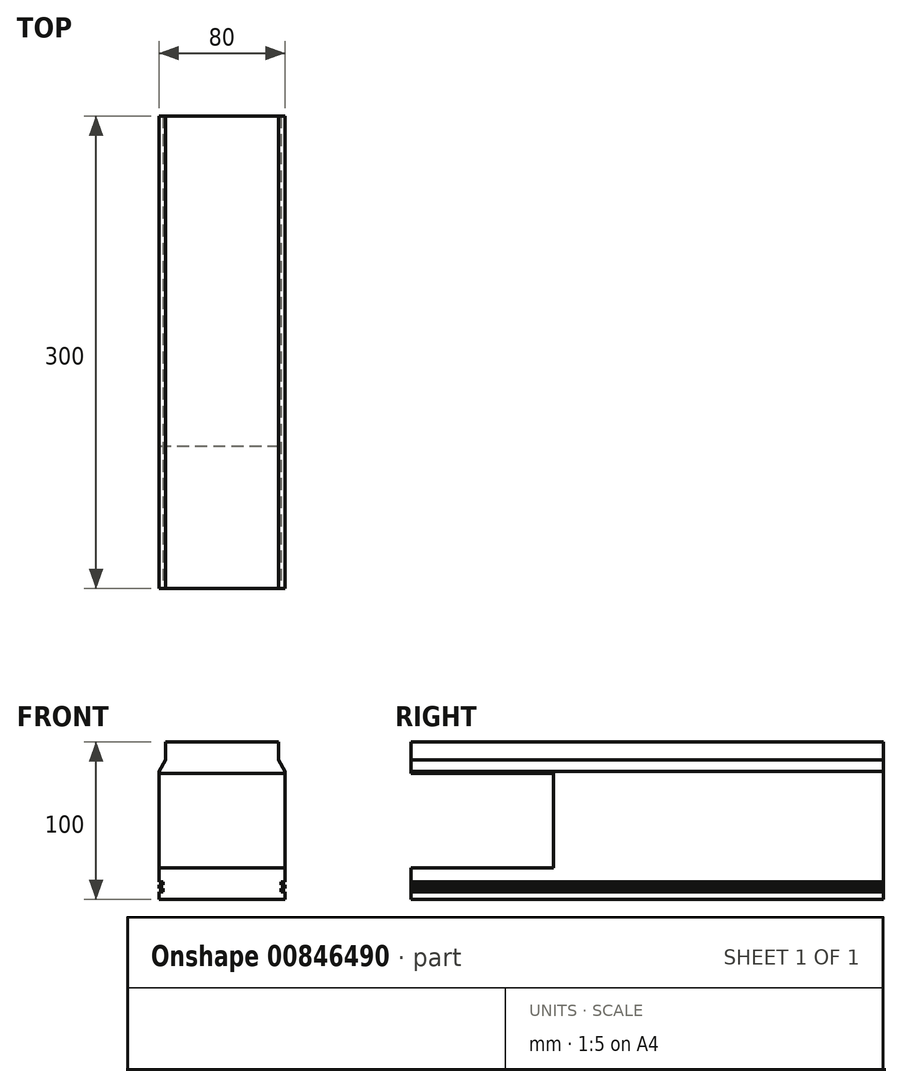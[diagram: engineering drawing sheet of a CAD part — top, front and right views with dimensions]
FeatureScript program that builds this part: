
annotation { "Feature Type Name" : "Feature", "Feature Type Description" : "" }
export const myFeature = defineFeature(function(context is Context, id is Id, definition is map)
    precondition{}
    {
        {
            var Q0;
            Q0=qCreatedBy(makeId("Top.planeOp"),FACE);
            var sketch = newSketch(context, id + "F0", { "sketchPlane" : qUnion([Q0])});
            skLineSegment(sketch, "E0.bottom", {"start": v(40, 150) * mm, "end": v(-40, 150) * mm});
            skLineSegment(sketch, "E0.top", {"start": v(40, -150) * mm, "end": v(-40, -150) * mm});
            skLineSegment(sketch, "E0.left", {"start": v(40, 150) * mm, "end": v(40, -150) * mm});
            skLineSegment(sketch, "E0.right", {"start": v(-40, 150) * mm, "end": v(-40, -150) * mm});
            skPoint(sketch, "E0.middle", {"position": v(0, 0) * mm});
            skSolve(sketch);
        }
        {
            var Q0;
            Q0=makeQuery(id+"F0.imprint","IMPRINT",FACE,{"disambiguationData":[TD([[makeQuery(id+"F0.imprint","IMPRINT",EDGE,{"derivedFrom":sQuery(id+"F0.wireOp",EDGE,"E0.bottom")}),1.0]])]});
            extrude(context, id + "F1", {"entities" : qUnion([Q0]), "depth" : 100 * mm, "offsetDistance" : 25 * mm});
        }
        {
            var Q0;
            Q0=makeQuery(id+"F1.opExtrude","SWEPT_FACE",FACE,{"disambiguationData":[OSD([sQuery(id+"F0.wireOp",EDGE,"E0.top")])]});
            var sketch = newSketch(context, id + "F2", { "sketchPlane" : qUnion([Q0])});
            skLineSegment(sketch, "E1", {"start": v(35.78, 100) * mm, "end": v(35.78, 88.74) * mm});
            skLineSegment(sketch, "E2", {"start": v(35.78, 88.74) * mm, "end": v(40, 81.33) * mm});
            skLineSegment(sketch, "E3", {"start": v(40, 81.33) * mm, "end": v(40, 60.77) * mm});
            skLineSegment(sketch, "E4", {"start": v(40, 60.77) * mm, "end": v(37.4, 60.77) * mm});
            skLineSegment(sketch, "E5", {"start": v(37.4, 60.77) * mm, "end": v(37.4, 31.01) * mm});
            skLineSegment(sketch, "E6", {"start": v(37.4, 31.01) * mm, "end": v(40, 31.01) * mm});
            skLineSegment(sketch, "E7", {"start": v(40, 31.01) * mm, "end": v(40, 0) * mm});
            skLineSegment(sketch, "E8", {"start": v(40, 0) * mm, "end": v(-40, 0) * mm});
            skLineSegment(sketch, "E9.MirrorCS", {"start": v(-35.78, 100) * mm, "end": v(-35.78, 88.74) * mm});
            skLineSegment(sketch, "E10.MirrorCS", {"start": v(-35.78, 88.74) * mm, "end": v(-40, 81.33) * mm});
            skLineSegment(sketch, "E11.MirrorCS", {"start": v(-40, 81.33) * mm, "end": v(-40, 60.77) * mm});
            skLineSegment(sketch, "E12.MirrorCS", {"start": v(-40, 60.77) * mm, "end": v(-37.4, 60.77) * mm});
            skLineSegment(sketch, "E13.MirrorCS", {"start": v(-37.4, 60.77) * mm, "end": v(-37.4, 31.01) * mm});
            skLineSegment(sketch, "E14.MirrorCS", {"start": v(-37.4, 31.01) * mm, "end": v(-40, 31.01) * mm});
            skLineSegment(sketch, "E15.MirrorCS", {"start": v(-40, 31.01) * mm, "end": v(-40, 0) * mm});
            skLineSegment(sketch, "E16.MirrorCS", {"start": v(-40, 0) * mm, "end": v(40, 0) * mm});
            skLineSegment(sketch, "E17", {"start": v(-40, 28.04) * mm, "end": v(-37.4, 28.04) * mm});
            skLineSegment(sketch, "E18", {"start": v(-37.4, 28.04) * mm, "end": v(-37.4, 25.93) * mm});
            skLineSegment(sketch, "E19", {"start": v(-37.4, 25.93) * mm, "end": v(-40, 25.93) * mm});
            skLineSegment(sketch, "E20.MirrorCS", {"start": v(-40, 23.83) * mm, "end": v(-37.4, 23.83) * mm});
            skLineSegment(sketch, "E21.MirrorCS", {"start": v(-37.4, 21.72) * mm, "end": v(-40, 21.72) * mm});
            skLineSegment(sketch, "E22.MirrorCS", {"start": v(-40, 19.62) * mm, "end": v(-37.4, 19.62) * mm});
            skLineSegment(sketch, "E23.MirrorCS", {"start": v(-37.4, 23.83) * mm, "end": v(-37.4, 21.72) * mm});
            skLineSegment(sketch, "E24.MirrorCS", {"start": v(-37.4, 17.51) * mm, "end": v(-40, 17.51) * mm});
            skLineSegment(sketch, "E25.MirrorCS", {"start": v(-40, 15.4) * mm, "end": v(-37.4, 15.4) * mm});
            skLineSegment(sketch, "E26.MirrorCS", {"start": v(-37.4, 13.3) * mm, "end": v(-40, 13.3) * mm});
            skLineSegment(sketch, "E27.MirrorCS", {"start": v(-40, 11.2) * mm, "end": v(-37.4, 11.2) * mm});
            skLineSegment(sketch, "E28.MirrorCS", {"start": v(-37.4, 15.4) * mm, "end": v(-37.4, 13.3) * mm});
            skLineSegment(sketch, "E29.MirrorCS", {"start": v(-37.4, 19.62) * mm, "end": v(-37.4, 17.51) * mm});
            skLineSegment(sketch, "E30.MirrorCS", {"start": v(-37.4, 9.1) * mm, "end": v(-40, 9.1) * mm});
            skLineSegment(sketch, "E31.MirrorCS", {"start": v(-40, 7) * mm, "end": v(-37.4, 7) * mm});
            skLineSegment(sketch, "E32.MirrorCS", {"start": v(-37.4, 4.89) * mm, "end": v(-40, 4.89) * mm});
            skLineSegment(sketch, "E33.MirrorCS", {"start": v(-37.4, 11.2) * mm, "end": v(-37.4, 9.1) * mm});
            skLineSegment(sketch, "E34.MirrorCS", {"start": v(-37.4, 7) * mm, "end": v(-37.4, 4.89) * mm});
            skPoint(sketch, "E35.MirrorCS.end.orphan", {"position": v(-37.4, 25.93) * mm});
            skPoint(sketch, "E35.MirrorCS.start.orphan", {"position": v(-37.4, 23.83) * mm});
            skPoint(sketch, "E36.MirrorCS.end.orphan", {"position": v(-37.4, 21.72) * mm});
            skPoint(sketch, "E36.MirrorCS.start.orphan", {"position": v(-37.4, 19.62) * mm});
            skPoint(sketch, "E37.MirrorCS.end.orphan", {"position": v(-37.4, 17.51) * mm});
            skPoint(sketch, "E37.MirrorCS.start.orphan", {"position": v(-37.4, 15.4) * mm});
            skPoint(sketch, "E38.MirrorCS.end.orphan", {"position": v(-37.4, 13.3) * mm});
            skPoint(sketch, "E38.MirrorCS.start.orphan", {"position": v(-37.4, 11.2) * mm});
            skPoint(sketch, "E39.MirrorCS.end.orphan", {"position": v(-37.4, 9.1) * mm});
            skPoint(sketch, "E39.MirrorCS.start.orphan", {"position": v(-37.4, 7) * mm});
            skLineSegment(sketch, "E40.MirrorCS", {"start": v(37.4, 4.89) * mm, "end": v(40, 4.89) * mm});
            skLineSegment(sketch, "E41.MirrorCS", {"start": v(37.4, 7) * mm, "end": v(37.4, 4.89) * mm});
            skLineSegment(sketch, "E42.MirrorCS", {"start": v(40, 7) * mm, "end": v(37.4, 7) * mm});
            skLineSegment(sketch, "E43.MirrorCS", {"start": v(37.4, 9.1) * mm, "end": v(40, 9.1) * mm});
            skLineSegment(sketch, "E44.MirrorCS", {"start": v(37.4, 11.2) * mm, "end": v(37.4, 9.1) * mm});
            skLineSegment(sketch, "E45.MirrorCS", {"start": v(37.4, 13.3) * mm, "end": v(40, 13.3) * mm});
            skPoint(sketch, "E46.MirrorP", {"position": v(37.4, 13.3) * mm});
            skPoint(sketch, "E47.MirrorP", {"position": v(37.4, 15.4) * mm});
            skLineSegment(sketch, "E48.MirrorCS", {"start": v(37.4, 15.4) * mm, "end": v(37.4, 13.3) * mm});
            skLineSegment(sketch, "E49.MirrorCS", {"start": v(40, 15.4) * mm, "end": v(37.4, 15.4) * mm});
            skLineSegment(sketch, "E50.MirrorCS", {"start": v(37.4, 17.51) * mm, "end": v(40, 17.51) * mm});
            skLineSegment(sketch, "E51.MirrorCS", {"start": v(37.4, 19.62) * mm, "end": v(37.4, 17.51) * mm});
            skLineSegment(sketch, "E52.MirrorCS", {"start": v(40, 19.62) * mm, "end": v(37.4, 19.62) * mm});
            skLineSegment(sketch, "E53.MirrorCS", {"start": v(37.4, 21.72) * mm, "end": v(40, 21.72) * mm});
            skLineSegment(sketch, "E54.MirrorCS", {"start": v(40, 23.83) * mm, "end": v(37.4, 23.83) * mm});
            skLineSegment(sketch, "E55.MirrorCS", {"start": v(37.4, 23.83) * mm, "end": v(37.4, 21.72) * mm});
            skLineSegment(sketch, "E56.MirrorCS", {"start": v(37.4, 25.93) * mm, "end": v(40, 25.93) * mm});
            skLineSegment(sketch, "E57.MirrorCS", {"start": v(37.4, 28.04) * mm, "end": v(37.4, 25.93) * mm});
            skLineSegment(sketch, "E58.MirrorCS", {"start": v(40, 28.04) * mm, "end": v(37.4, 28.04) * mm});
            skLineSegment(sketch, "E59.MirrorCS", {"start": v(40, 11.2) * mm, "end": v(37.4, 11.2) * mm});
            skSolve(sketch);
        }
        {
            var Q0;
            Q0=makeQuery(id+"F1.opExtrude","SWEPT_FACE",FACE,{"disambiguationData":[OSD([sQuery(id+"F0.wireOp",EDGE,"E0.left")])]});
            var sketch = newSketch(context, id + "F3", { "sketchPlane" : qUnion([Q0])});
            skLineSegment(sketch, "E60.bottom", {"start": v(-59.49, 80.07) * mm, "end": v(-240.51, 80.07) * mm});
            skLineSegment(sketch, "E60.top", {"start": v(-59.49, 19.93) * mm, "end": v(-240.51, 19.93) * mm});
            skLineSegment(sketch, "E60.left", {"start": v(-59.49, 80.07) * mm, "end": v(-59.49, 19.93) * mm});
            skLineSegment(sketch, "E60.right", {"start": v(-240.51, 80.07) * mm, "end": v(-240.51, 19.93) * mm});
            skPoint(sketch, "E60.middle", {"position": v(-150, 50) * mm});
            skSolve(sketch);
        }
        {
            var Q0;
            {var subQ0=sQuery(id+"F3.wireOp",EDGE,"E60.left");Q0=makeQuery(id+"F3.imprint","IMPRINT",FACE,{"disambiguationData":[TD([[makeQuery(id+"F3.imprint","IMPRINT",EDGE,{"derivedFrom":subQ0}),-1.0]])]});}
            extrude(context, id + "F4", {"entities" : qUnion([Q0]), "operationType" : NewBodyOperationType.REMOVE, "oppositeDirection" : true, "depth" : 128 * mm, "offsetDistance" : 25 * mm});
        }
        {
            var Q0;
            {var subQ0=sQuery(id+"F2.wireOp",EDGE,"E1");Q0=makeQuery(id+"F2.imprint","IMPRINT",FACE,{"disambiguationData":[TD([[makeQuery(id+"F2.imprint","IMPRINT",EDGE,{"derivedFrom":subQ0}),1.0]])]});}
            var Q1;
            {var subQ0=sQuery(id+"F2.wireOp",EDGE,"E9.MirrorCS");Q1=makeQuery(id+"F2.imprint","IMPRINT",FACE,{"disambiguationData":[TD([[makeQuery(id+"F2.imprint","IMPRINT",EDGE,{"derivedFrom":subQ0}),-1.0]])]});}
            var Q2;
            {var subQ0=sQuery(id+"F2.wireOp",EDGE,"E43.MirrorCS");Q2=makeQuery(id+"F2.imprint","IMPRINT",FACE,{"disambiguationData":[TD([[makeQuery(id+"F2.imprint","IMPRINT",EDGE,{"derivedFrom":subQ0}),1.0]])]});}
            var Q3;
            {var subQ0=sQuery(id+"F2.wireOp",EDGE,"E40.MirrorCS");Q3=makeQuery(id+"F2.imprint","IMPRINT",FACE,{"disambiguationData":[TD([[makeQuery(id+"F2.imprint","IMPRINT",EDGE,{"derivedFrom":subQ0}),1.0]])]});}
            var Q4;
            {var subQ0=sQuery(id+"F2.wireOp",EDGE,"E31.MirrorCS");Q4=makeQuery(id+"F2.imprint","IMPRINT",FACE,{"disambiguationData":[TD([[makeQuery(id+"F2.imprint","IMPRINT",EDGE,{"derivedFrom":subQ0}),-1.0]])]});}
            var Q5;
            {var subQ0=sQuery(id+"F2.wireOp",EDGE,"E27.MirrorCS");Q5=makeQuery(id+"F2.imprint","IMPRINT",FACE,{"disambiguationData":[TD([[makeQuery(id+"F2.imprint","IMPRINT",EDGE,{"derivedFrom":subQ0}),-1.0]])]});}
            extrude(context, id + "F5", {"entities" : qUnion([Q0, Q1, Q2, Q3, Q4, Q5]), "operationType" : NewBodyOperationType.REMOVE, "oppositeDirection" : true, "depth" : 322.9 * mm, "offsetDistance" : 25 * mm});
        }
    });
